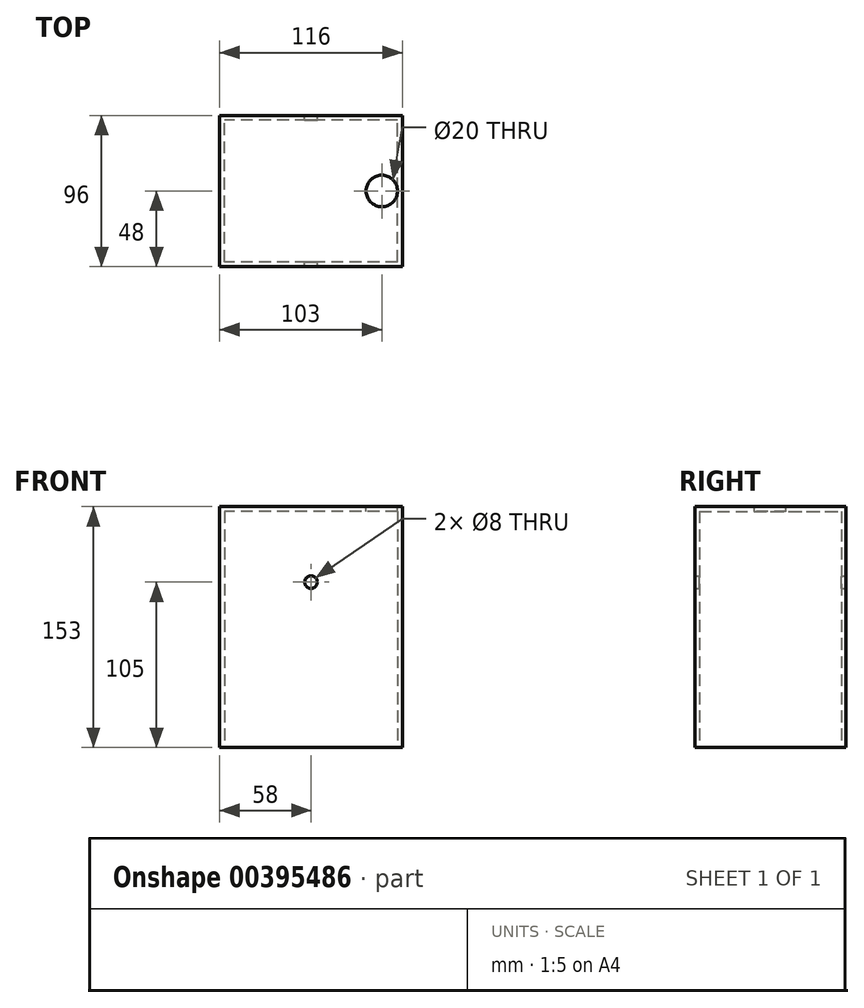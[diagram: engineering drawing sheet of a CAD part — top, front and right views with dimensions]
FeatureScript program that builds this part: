
annotation { "Feature Type Name" : "Feature", "Feature Type Description" : "" }
export const myFeature = defineFeature(function(context is Context, id is Id, definition is map)
    precondition{}
    {
        {
            var Q0;
            Q0=qCreatedBy(makeId("Top.planeOp"),FACE);
            var sketch = newSketch(context, id + "F0", { "sketchPlane" : qUnion([Q0])});
            skLineSegment(sketch, "E0.bottom", {"start": v(55, -45) * mm, "end": v(-55, -45) * mm});
            skLineSegment(sketch, "E0.top", {"start": v(55, 45) * mm, "end": v(-55, 45) * mm});
            skLineSegment(sketch, "E0.left", {"start": v(55, -45) * mm, "end": v(55, 45) * mm});
            skLineSegment(sketch, "E0.right", {"start": v(-55, -45) * mm, "end": v(-55, 45) * mm});
            skPoint(sketch, "E0.middle", {"position": v(0, 0) * mm});
            skSolve(sketch);
        }
        {
            var Q0;
            Q0 = qSketchRegion(id + "F0", true);
            extrude(context, id + "F1", {"entities" : qUnion([Q0]), "endBound" : BoundingType.SYMMETRIC, "depth" : 150 * mm, "offsetDistance" : 25.4 * mm});
        }
        {
            var Q0;
            Q0=makeQuery(id+"F1.opExtrude","CAP_FACE",FACE,{"disambiguationData":[OSD([sQuery(id+"F0.wireOp",EDGE,"E0.bottom"),sQuery(id+"F0.wireOp",EDGE,"E0.top"),sQuery(id+"F0.wireOp",EDGE,"E0.left"),sQuery(id+"F0.wireOp",EDGE,"E0.right")])],"isStart":true});
            shell(context, id + "F2", {"entities" : qUnion([Q0]), "thickness" : 3 * mm, "oppositeDirection" : true});
        }
        {
            var Q0;
            Q0=makeQuery(id+"F1.opExtrude","CAP_FACE",FACE,{"disambiguationData":[OSD([sQuery(id+"F0.wireOp",EDGE,"E0.bottom"),sQuery(id+"F0.wireOp",EDGE,"E0.top"),sQuery(id+"F0.wireOp",EDGE,"E0.left"),sQuery(id+"F0.wireOp",EDGE,"E0.right")])],"isStart":false});
            var sketch = newSketch(context, id + "F3", { "sketchPlane" : qUnion([Q0])});
            skLineSegment(sketch, "E1.left", {"start": v(35, -35) * mm, "end": v(35, -34.97) * mm});
            skPoint(sketch, "E1.middle", {"position": v(0, 0) * mm});
            skLineSegment(sketch, "E2.trimOffspring", {"start": v(35, 34.97) * mm, "end": v(35, 35) * mm});
            skLineSegment(sketch, "E3", {"start": v(35, 35) * mm, "end": v(35, 34.97) * mm});
            skLineSegment(sketch, "E4.0.0", {"start": v(58, -48) * mm, "end": v(58, 48) * mm});
            skLineSegment(sketch, "E4.0.1", {"start": v(58, 48) * mm, "end": v(-58, 48) * mm});
            skLineSegment(sketch, "E4.0.2", {"start": v(-58, 48) * mm, "end": v(-58, -48) * mm});
            skLineSegment(sketch, "E4.0.3", {"start": v(-58, -48) * mm, "end": v(58, -48) * mm});
            skPoint(sketch, "E5.start.orphan", {"position": v(58, 0) * mm});
            skLineSegment(sketch, "E6", {"start": v(58, 0) * mm, "end": v(55, 0) * mm});
            skLineSegment(sketch, "E7", {"start": v(55, 0) * mm, "end": v(55, -10) * mm});
            skLineSegment(sketch, "E8", {"start": v(55, -10) * mm, "end": v(35, -10) * mm});
            skLineSegment(sketch, "E9", {"start": v(35, -10) * mm, "end": v(35, 10) * mm});
            skLineSegment(sketch, "E10", {"start": v(35, 10) * mm, "end": v(55, 10) * mm});
            skLineSegment(sketch, "E11", {"start": v(55, 10) * mm, "end": v(55, 0) * mm});
            skPoint(sketch, "E12.start.orphan", {"position": v(0, 48) * mm});
            skCircle(sketch, "E13", {"center": v(45, 0) * mm, "radius": 10 * mm});
            skPoint(sketch, "E14.orphan", {"position": v(45, 10) * mm});
            skPoint(sketch, "E15.end.orphan", {"position": v(45, -10) * mm});
            skSolve(sketch);
        }
        {
            var Q0;
            {var subQ0=sQuery(id+"F3.wireOp",EDGE,"E13");var subQ3=makeQuery(id+"F3.imprint","INTERSECT",VERTEX,{"derivedFrom":[sQuery(id+"F3.wireOp",EDGE,"E9"),subQ0]});Q0=makeQuery(id+"F3.imprint","IMPRINT",FACE,{"disambiguationData":[TD([[makeQuery(id+"F3.imprint","IMPRINT",EDGE,{"disambiguationData":[TD([[subQ3,1.0]])],"derivedFrom":subQ0}),1.0]])]});}
            extrude(context, id + "F4", {"entities" : qUnion([Q0]), "operationType" : NewBodyOperationType.REMOVE, "oppositeDirection" : true, "depth" : 25.4 * mm, "offsetDistance" : 25.4 * mm});
        }
        {
            var Q0;
            Q0=makeQuery(id+"F2.opShell","OFFSET_FACE",FACE,{"disambiguationData":[OSD([sQuery(id+"F0.wireOp",EDGE,"E0.bottom")])]});
            var sketch = newSketch(context, id + "F5", { "sketchPlane" : qUnion([Q0])});
            skLineSegment(sketch, "E16.0.0", {"start": v(-58, -75) * mm, "end": v(58, -75) * mm});
            skLineSegment(sketch, "E16.0.1", {"start": v(58, -75) * mm, "end": v(58, 78) * mm});
            skLineSegment(sketch, "E16.0.2", {"start": v(58, 78) * mm, "end": v(-58, 78) * mm});
            skLineSegment(sketch, "E16.0.3", {"start": v(-58, 78) * mm, "end": v(-58, -75) * mm});
            skLineSegment(sketch, "E17", {"start": v(0, -75) * mm, "end": v(0, 30) * mm});
            skCircle(sketch, "E18", {"center": v(0, 30) * mm, "radius": 4 * mm});
            skSolve(sketch);
        }
        {
            var Q0;
            Q0=makeQuery(id+"F5.imprint","IMPRINT",FACE,{"disambiguationData":[TD([[makeQuery(id+"F5.imprint","IMPRINT",EDGE,{"derivedFrom":sQuery(id+"F5.wireOp",EDGE,"E18")}),1.0]])]});
            extrude(context, id + "F6", {"entities" : qUnion([Q0]), "operationType" : NewBodyOperationType.REMOVE, "oppositeDirection" : true, "depth" : 25.4 * mm, "offsetDistance" : 25.4 * mm, "hasSecondDirection" : true, "secondDirectionOppositeDirection" : false, "secondDirectionDepth" : 126.75 * mm});
        }
    });
